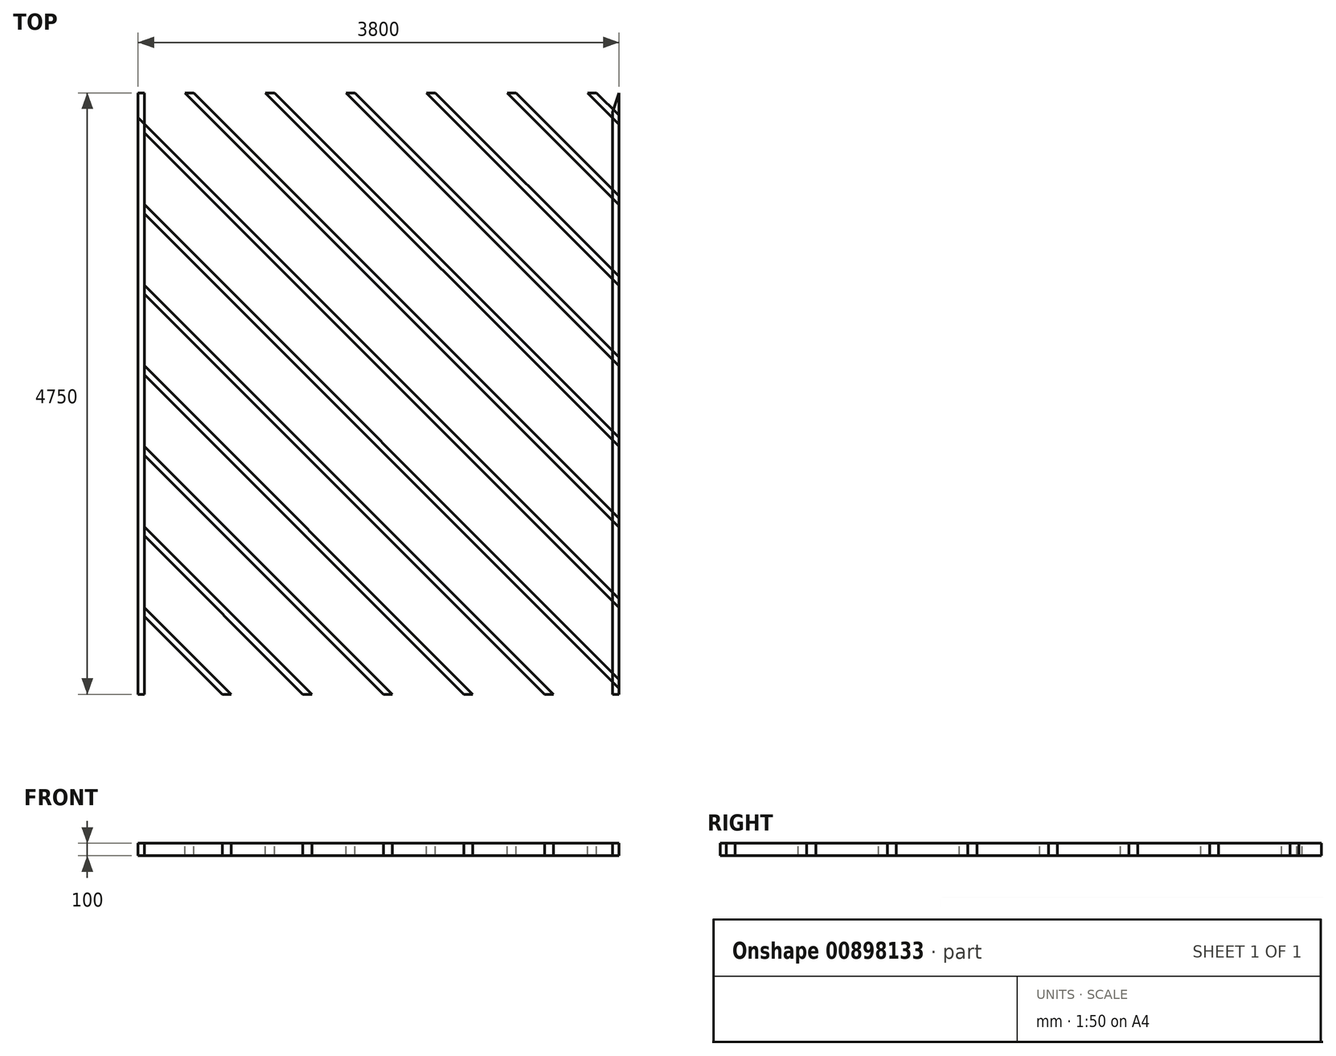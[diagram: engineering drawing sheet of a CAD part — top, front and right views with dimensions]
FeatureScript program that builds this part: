
annotation { "Feature Type Name" : "Feature", "Feature Type Description" : "" }
export const myFeature = defineFeature(function(context is Context, id is Id, definition is map)
    precondition{}
    {
        {
            var Q0;
            Q0=qCreatedBy(makeId("Top.planeOp"),FACE);
            var sketch = newSketch(context, id + "F0", { "sketchPlane" : qUnion([Q0])});
            skLineSegment(sketch, "E0", {"start": v(-2451.02, -4769.13) * mm, "end": v(-2451.02, -19.13) * mm});
            skLineSegment(sketch, "E1", {"start": v(-2451.02, -19.13) * mm, "end": v(-2451.02, 3650.87) * mm});
            skLineSegment(sketch, "E2", {"start": v(-2451.02, 3650.87) * mm, "end": v(2548.98, 3650.87) * mm});
            skLineSegment(sketch, "E3", {"start": v(2548.98, 3650.87) * mm, "end": v(1348.98, -19.13) * mm});
            skLineSegment(sketch, "E4", {"start": v(1348.98, -19.13) * mm, "end": v(-2451.02, -19.13) * mm});
            skLineSegment(sketch, "E5", {"start": v(-2451.02, -4769.13) * mm, "end": v(1348.98, -4769.13) * mm});
            skLineSegment(sketch, "E6", {"start": v(1348.98, -4769.13) * mm, "end": v(1348.98, -19.13) * mm});
            skSolve(sketch);
        }
        {
            var Q0;
            Q0=makeQuery(id+"F0.imprint","IMPRINT",FACE,{"disambiguationData":[TD([[makeQuery(id+"F0.imprint","IMPRINT",EDGE,{"derivedFrom":sQuery(id+"F0.wireOp",EDGE,"E0")}),-1.0]])]});
            var sketch = newSketch(context, id + "F1", { "sketchPlane" : qUnion([Q0])});
            skLineSegment(sketch, "E7.bottom", {"start": v(-2451.02, -19.13) * mm, "end": v(-2401.02, -19.13) * mm});
            skLineSegment(sketch, "E7.top", {"start": v(-2451.02, -4769.13) * mm, "end": v(-2401.02, -4769.13) * mm});
            skLineSegment(sketch, "E7.left", {"start": v(-2451.02, -19.13) * mm, "end": v(-2451.02, -4769.13) * mm});
            skLineSegment(sketch, "E7.right", {"start": v(-2401.02, -19.13) * mm, "end": v(-2401.02, -4769.13) * mm});
            skLineSegment(sketch, "E8.bottom", {"start": v(1348.98, -4769.13) * mm, "end": v(1298.98, -4769.13) * mm});
            skLineSegment(sketch, "E8.top", {"start": v(1348.98, -19.13) * mm, "end": v(1298.98, -19.13) * mm});
            skLineSegment(sketch, "E8.left", {"start": v(1348.98, -4769.13) * mm, "end": v(1348.98, -19.13) * mm});
            skLineSegment(sketch, "E8.right", {"start": v(1298.98, -4769.13) * mm, "end": v(1298.98, -19.13) * mm});
            skLineSegment(sketch, "E9.bottom", {"start": v(-2401.02, -4769.13) * mm, "end": v(1298.98, -4769.13) * mm});
            skLineSegment(sketch, "E9.top", {"start": v(-2401.02, -4719.13) * mm, "end": v(1298.98, -4719.13) * mm});
            skLineSegment(sketch, "E9.left", {"start": v(-2401.02, -4769.13) * mm, "end": v(-2401.02, -4719.13) * mm});
            skLineSegment(sketch, "E9.right", {"start": v(1298.98, -4769.13) * mm, "end": v(1298.98, -4719.13) * mm});
            skLineSegment(sketch, "E10.bottom", {"start": v(-2401.02, -19.13) * mm, "end": v(1298.98, -19.13) * mm});
            skLineSegment(sketch, "E10.top", {"start": v(-2401.02, -69.13) * mm, "end": v(1298.98, -69.13) * mm});
            skLineSegment(sketch, "E10.left", {"start": v(-2401.02, -19.13) * mm, "end": v(-2401.02, -69.13) * mm});
            skLineSegment(sketch, "E10.right", {"start": v(1298.98, -19.13) * mm, "end": v(1298.98, -69.13) * mm});
            skLineSegment(sketch, "E11.top", {"start": v(-2451.02, 3650.87) * mm, "end": v(-2401.02, 3650.87) * mm});
            skLineSegment(sketch, "E11.left", {"start": v(-2451.02, -19.13) * mm, "end": v(-2451.02, 3650.87) * mm});
            skLineSegment(sketch, "E11.right", {"start": v(-2401.02, -19.13) * mm, "end": v(-2401.02, 3650.87) * mm});
            skLineSegment(sketch, "E12.bottom", {"start": v(-2401.02, 3650.87) * mm, "end": v(2398.98, 3650.87) * mm});
            skLineSegment(sketch, "E12.top", {"start": v(-2401.02, 3600.87) * mm, "end": v(2398.98, 3600.87) * mm});
            skLineSegment(sketch, "E12.left", {"start": v(-2401.02, 3650.87) * mm, "end": v(-2401.02, 3600.87) * mm});
            skLineSegment(sketch, "E12.right", {"start": v(2398.98, 3650.87) * mm, "end": v(2398.98, 3600.87) * mm});
            skLineSegment(sketch, "E13.top", {"start": v(-2401.02, 30.87) * mm, "end": v(1298.98, 30.87) * mm});
            skLineSegment(sketch, "E13.left", {"start": v(-2401.02, -19.13) * mm, "end": v(-2401.02, 30.87) * mm});
            skLineSegment(sketch, "E13.right", {"start": v(1298.98, -19.13) * mm, "end": v(1298.98, 30.87) * mm});
            skLineSegment(sketch, "E14", {"start": v(2611.65, 4003.42) * mm, "end": v(1119.9, -558.89) * mm});
            skLineSegment(sketch, "E15", {"start": v(1119.9, -558.89) * mm, "end": v(1167.42, -574.43) * mm});
            skLineSegment(sketch, "E16", {"start": v(1167.42, -574.43) * mm, "end": v(2659.18, 3987.88) * mm});
            skLineSegment(sketch, "E17", {"start": v(2659.18, 3987.88) * mm, "end": v(2611.65, 4003.42) * mm});
            skSolve(sketch);
        }
        {
            var Q0;
            Q0=makeQuery(id+"F0.imprint","IMPRINT",FACE,{"disambiguationData":[TD([[makeQuery(id+"F0.imprint","IMPRINT",EDGE,{"derivedFrom":sQuery(id+"F0.wireOp",EDGE,"E0")}),-1.0]])]});
            var sketch = newSketch(context, id + "F2", { "sketchPlane" : qUnion([Q0])});
            skLineSegment(sketch, "E18", {"start": v(-2451.02, -4103.44) * mm, "end": v(-1785.33, -4769.13) * mm});
            skLineSegment(sketch, "E19", {"start": v(-1714.62, -4769.13) * mm, "end": v(-2451.02, -4032.73) * mm});
            skLineSegment(sketch, "E20", {"start": v(-2401.02, -19.13) * mm, "end": v(-2401.02, -69.13) * mm});
            skLineSegment(sketch, "E21", {"start": v(-2401.02, -19.13) * mm, "end": v(-2451.02, -19.13) * mm});
            skLineSegment(sketch, "E22", {"start": v(-2451.02, -4769.13) * mm, "end": v(-2451.02, -19.13) * mm});
            skLineSegment(sketch, "E23", {"start": v(-2451.02, -4769.13) * mm, "end": v(-2401.02, -4769.13) * mm});
            skLineSegment(sketch, "E24", {"start": v(-2401.02, -4719.13) * mm, "end": v(-2401.02, -4769.13) * mm});
            skLineSegment(sketch, "E25", {"start": v(-2401.02, -69.13) * mm, "end": v(-2401.02, -4719.13) * mm});
            skLineSegment(sketch, "E26", {"start": v(1348.98, -4769.13) * mm, "end": v(1348.98, -19.13) * mm});
            skLineSegment(sketch, "E27", {"start": v(1348.98, -19.13) * mm, "end": v(-2451.02, -19.13) * mm});
            skLineSegment(sketch, "E28", {"start": v(-2451.02, -4769.13) * mm, "end": v(1348.98, -4769.13) * mm});
            skLineSegment(sketch, "E29", {"start": v(-2451.02, -3467.05) * mm, "end": v(-1148.93, -4769.13) * mm});
            skLineSegment(sketch, "E30", {"start": v(-1078.22, -4769.13) * mm, "end": v(-2451.02, -3396.34) * mm});
            skLineSegment(sketch, "E31", {"start": v(-2451.02, -2830.65) * mm, "end": v(-512.54, -4769.13) * mm});
            skLineSegment(sketch, "E32", {"start": v(-441.83, -4769.13) * mm, "end": v(-2451.02, -2759.94) * mm});
            skLineSegment(sketch, "E33", {"start": v(-2451.02, -2194.26) * mm, "end": v(123.86, -4769.13) * mm});
            skLineSegment(sketch, "E34", {"start": v(194.57, -4769.13) * mm, "end": v(-2451.02, -2123.55) * mm});
            skLineSegment(sketch, "E35", {"start": v(-2451.02, -1557.86) * mm, "end": v(760.25, -4769.13) * mm});
            skLineSegment(sketch, "E36", {"start": v(830.96, -4769.13) * mm, "end": v(-2451.02, -1487.15) * mm});
            skLineSegment(sketch, "E37", {"start": v(-2451.02, -921.46) * mm, "end": v(1348.98, -4721.46) * mm});
            skLineSegment(sketch, "E38", {"start": v(-2451.02, -850.75) * mm, "end": v(1348.98, -4650.75) * mm});
            skLineSegment(sketch, "E39", {"start": v(-2451.02, -285.07) * mm, "end": v(1348.98, -4085.07) * mm});
            skLineSegment(sketch, "E40", {"start": v(1348.98, -4014.36) * mm, "end": v(-2451.02, -214.36) * mm});
            skLineSegment(sketch, "E41", {"start": v(-2080.56, -19.13) * mm, "end": v(1348.98, -3448.67) * mm});
            skLineSegment(sketch, "E42", {"start": v(1348.98, -3377.96) * mm, "end": v(-2009.85, -19.13) * mm});
            skLineSegment(sketch, "E43", {"start": v(-1444.16, -19.13) * mm, "end": v(1348.98, -2812.28) * mm});
            skLineSegment(sketch, "E44", {"start": v(1348.98, -2741.56) * mm, "end": v(-1373.45, -19.13) * mm});
            skLineSegment(sketch, "E45", {"start": v(-807.77, -19.13) * mm, "end": v(1348.98, -2175.88) * mm});
            skLineSegment(sketch, "E46", {"start": v(1348.98, -2105.17) * mm, "end": v(-737.05, -19.13) * mm});
            skLineSegment(sketch, "E47", {"start": v(-171.37, -19.13) * mm, "end": v(1348.98, -1539.48) * mm});
            skLineSegment(sketch, "E48", {"start": v(1348.98, -1468.77) * mm, "end": v(-100.66, -19.13) * mm});
            skLineSegment(sketch, "E49", {"start": v(465.03, -19.13) * mm, "end": v(1348.98, -903.09) * mm});
            skLineSegment(sketch, "E50", {"start": v(1348.98, -832.38) * mm, "end": v(535.74, -19.13) * mm});
            skLineSegment(sketch, "E51", {"start": v(1101.42, -19.13) * mm, "end": v(1348.98, -266.7) * mm});
            skLineSegment(sketch, "E52", {"start": v(1348.98, -195.98) * mm, "end": v(1172.13, -19.13) * mm});
            skSolve(sketch);
        }
        {
            var Q0;
            {var subQ0=sQuery(id+"F2.wireOp",EDGE,"E20");Q0=makeQuery(id+"F2.imprint","IMPRINT",FACE,{"disambiguationData":[TD([[makeQuery(id+"F2.imprint","IMPRINT",EDGE,{"derivedFrom":subQ0}),-1.0]])]});}
            var Q1;
            {var subQ5=sQuery(id+"F1.wireOp",EDGE,"E9.left");Q1=makeQuery(id+"F1.imprint","IMPRINT",FACE,{"disambiguationData":[TD([[makeQuery(id+"F1.imprint","IMPRINT",EDGE,{"derivedFrom":subQ5}),-1.0]])]});}
            var Q2;
            {var subQ4=sQuery(id+"F1.wireOp",EDGE,"E7.top");Q2=makeQuery(id+"F1.imprint","IMPRINT",FACE,{"disambiguationData":[TD([[makeQuery(id+"F1.imprint","IMPRINT",EDGE,{"derivedFrom":subQ4}),1.0]])]});}
            var Q3;
            {var subQ0=sQuery(id+"F2.wireOp",EDGE,"E30");var subQ1=sQuery(id+"F2.wireOp",EDGE,"E25");var subQ2=makeQuery(id+"F2.imprint","INTERSECT",VERTEX,{"derivedFrom":[subQ1,subQ0]});Q3=makeQuery(id+"F2.imprint","IMPRINT",FACE,{"disambiguationData":[TD([[makeQuery(id+"F2.imprint","IMPRINT",EDGE,{"disambiguationData":[TD([[subQ2,-1.0]])],"derivedFrom":subQ1}),1.0]])]});}
            var Q4;
            {var subQ0=sQuery(id+"F2.wireOp",EDGE,"E34");var subQ1=sQuery(id+"F2.wireOp",EDGE,"E25");var subQ2=makeQuery(id+"F2.imprint","INTERSECT",VERTEX,{"derivedFrom":[subQ1,subQ0]});Q4=makeQuery(id+"F2.imprint","IMPRINT",FACE,{"disambiguationData":[TD([[makeQuery(id+"F2.imprint","IMPRINT",EDGE,{"disambiguationData":[TD([[subQ2,-1.0]])],"derivedFrom":subQ1}),1.0]])]});}
            var Q5;
            {var subQ0=sQuery(id+"F2.wireOp",EDGE,"E38");var subQ1=sQuery(id+"F2.wireOp",EDGE,"E25");var subQ2=makeQuery(id+"F2.imprint","INTERSECT",VERTEX,{"derivedFrom":[subQ1,subQ0]});Q5=makeQuery(id+"F2.imprint","IMPRINT",FACE,{"disambiguationData":[TD([[makeQuery(id+"F2.imprint","IMPRINT",EDGE,{"disambiguationData":[TD([[subQ2,-1.0]])],"derivedFrom":subQ1}),1.0]])]});}
            var Q6;
            {var subQ0=sQuery(id+"F2.wireOp",EDGE,"E28");var subQ1=sQuery(id+"F2.wireOp",EDGE,"E18");var subQ2=makeQuery(id+"F2.imprint","INTERSECT",VERTEX,{"derivedFrom":[subQ1,subQ0]});Q6=makeQuery(id+"F2.imprint","IMPRINT",FACE,{"disambiguationData":[TD([[makeQuery(id+"F2.imprint","IMPRINT",EDGE,{"disambiguationData":[TD([[subQ2,1.0]])],"derivedFrom":subQ1}),1.0]])]});}
            var Q7;
            {var subQ0=sQuery(id+"F2.wireOp",EDGE,"E32");var subQ1=sQuery(id+"F2.wireOp",EDGE,"E25");var subQ2=makeQuery(id+"F2.imprint","INTERSECT",VERTEX,{"derivedFrom":[subQ1,subQ0]});Q7=makeQuery(id+"F2.imprint","IMPRINT",FACE,{"disambiguationData":[TD([[makeQuery(id+"F2.imprint","IMPRINT",EDGE,{"disambiguationData":[TD([[subQ2,-1.0]])],"derivedFrom":subQ1}),1.0]])]});}
            var Q8;
            {var subQ0=sQuery(id+"F2.wireOp",EDGE,"E36");var subQ1=sQuery(id+"F2.wireOp",EDGE,"E25");var subQ2=makeQuery(id+"F2.imprint","INTERSECT",VERTEX,{"derivedFrom":[subQ1,subQ0]});Q8=makeQuery(id+"F2.imprint","IMPRINT",FACE,{"disambiguationData":[TD([[makeQuery(id+"F2.imprint","IMPRINT",EDGE,{"disambiguationData":[TD([[subQ2,-1.0]])],"derivedFrom":subQ1}),1.0]])]});}
            var Q9;
            {var subQ0=sQuery(id+"F2.wireOp",EDGE,"E40");var subQ1=sQuery(id+"F2.wireOp",EDGE,"E25");var subQ2=makeQuery(id+"F2.imprint","INTERSECT",VERTEX,{"derivedFrom":[subQ1,subQ0]});Q9=makeQuery(id+"F2.imprint","IMPRINT",FACE,{"disambiguationData":[TD([[makeQuery(id+"F2.imprint","IMPRINT",EDGE,{"disambiguationData":[TD([[subQ2,-1.0]])],"derivedFrom":subQ1}),1.0]])]});}
            var Q10;
            {var subQ0=sQuery(id+"F2.wireOp",EDGE,"E41");Q10=makeQuery(id+"F2.imprint","IMPRINT",FACE,{"disambiguationData":[TD([[makeQuery(id+"F2.imprint","IMPRINT",EDGE,{"derivedFrom":subQ0}),1.0]])]});}
            var Q11;
            {var subQ0=sQuery(id+"F2.wireOp",EDGE,"E43");Q11=makeQuery(id+"F2.imprint","IMPRINT",FACE,{"disambiguationData":[TD([[makeQuery(id+"F2.imprint","IMPRINT",EDGE,{"derivedFrom":subQ0}),1.0]])]});}
            var Q12;
            {var subQ0=sQuery(id+"F2.wireOp",EDGE,"E45");Q12=makeQuery(id+"F2.imprint","IMPRINT",FACE,{"disambiguationData":[TD([[makeQuery(id+"F2.imprint","IMPRINT",EDGE,{"derivedFrom":subQ0}),1.0]])]});}
            var Q13;
            {var subQ5=sQuery(id+"F1.wireOp",EDGE,"E10.left");Q13=makeQuery(id+"F1.imprint","IMPRINT",FACE,{"disambiguationData":[TD([[makeQuery(id+"F1.imprint","IMPRINT",EDGE,{"derivedFrom":subQ5}),1.0]])]});}
            var Q14;
            {var subQ0=sQuery(id+"F2.wireOp",EDGE,"E51");Q14=makeQuery(id+"F2.imprint","IMPRINT",FACE,{"disambiguationData":[TD([[makeQuery(id+"F2.imprint","IMPRINT",EDGE,{"derivedFrom":subQ0}),1.0]])]});}
            var Q15;
            {var subQ0=sQuery(id+"F2.wireOp",EDGE,"E49");Q15=makeQuery(id+"F2.imprint","IMPRINT",FACE,{"disambiguationData":[TD([[makeQuery(id+"F2.imprint","IMPRINT",EDGE,{"derivedFrom":subQ0}),1.0]])]});}
            var Q16;
            {var subQ0=sQuery(id+"F2.wireOp",EDGE,"E47");Q16=makeQuery(id+"F2.imprint","IMPRINT",FACE,{"disambiguationData":[TD([[makeQuery(id+"F2.imprint","IMPRINT",EDGE,{"derivedFrom":subQ0}),1.0]])]});}
            var Q17;
            {var subQ0=sQuery(id+"F1.wireOp",EDGE,"E9.bottom");var subQ1=sQuery(id+"F1.wireOp",EDGE,"E8.left");var subQ2=makeQuery(id+"F1.imprint","INTERSECT",VERTEX,{"derivedFrom":[subQ1,subQ0]});Q17=makeQuery(id+"F1.imprint","IMPRINT",FACE,{"disambiguationData":[TD([[makeQuery(id+"F1.imprint","IMPRINT",EDGE,{"disambiguationData":[TD([[subQ2,-1.0]])],"derivedFrom":subQ1}),1.0]])]});}
            var Q18;
            {var subQ0=sQuery(id+"F1.wireOp",EDGE,"E9.top");var subQ1=sQuery(id+"F1.wireOp",EDGE,"E8.left");var subQ2=makeQuery(id+"F1.imprint","INTERSECT",VERTEX,{"derivedFrom":[subQ1,subQ0]});Q18=makeQuery(id+"F1.imprint","IMPRINT",FACE,{"disambiguationData":[TD([[makeQuery(id+"F1.imprint","IMPRINT",EDGE,{"disambiguationData":[TD([[subQ2,-1.0]])],"derivedFrom":subQ1}),1.0]])]});}
            var Q19;
            {var subQ0=sQuery(id+"F1.wireOp",EDGE,"E10.bottom");var subQ1=sQuery(id+"F1.wireOp",EDGE,"E8.left");var subQ2=makeQuery(id+"F1.imprint","INTERSECT",VERTEX,{"derivedFrom":[subQ1,subQ0]});Q19=makeQuery(id+"F1.imprint","IMPRINT",FACE,{"disambiguationData":[TD([[makeQuery(id+"F1.imprint","IMPRINT",EDGE,{"disambiguationData":[TD([[subQ2,1.0]])],"derivedFrom":subQ1}),1.0]])]});}
            extrude(context, id + "F3", {"entities" : qUnion([Q0, Q1, Q2, Q3, Q4, Q5, Q6, Q7, Q8, Q9, Q10, Q11, Q12, Q13, Q14, Q15, Q16, Q17, Q18, Q19]), "oppositeDirection" : true, "depth" : 100 * mm, "offsetDistance" : 25 * mm});
        }
    });
